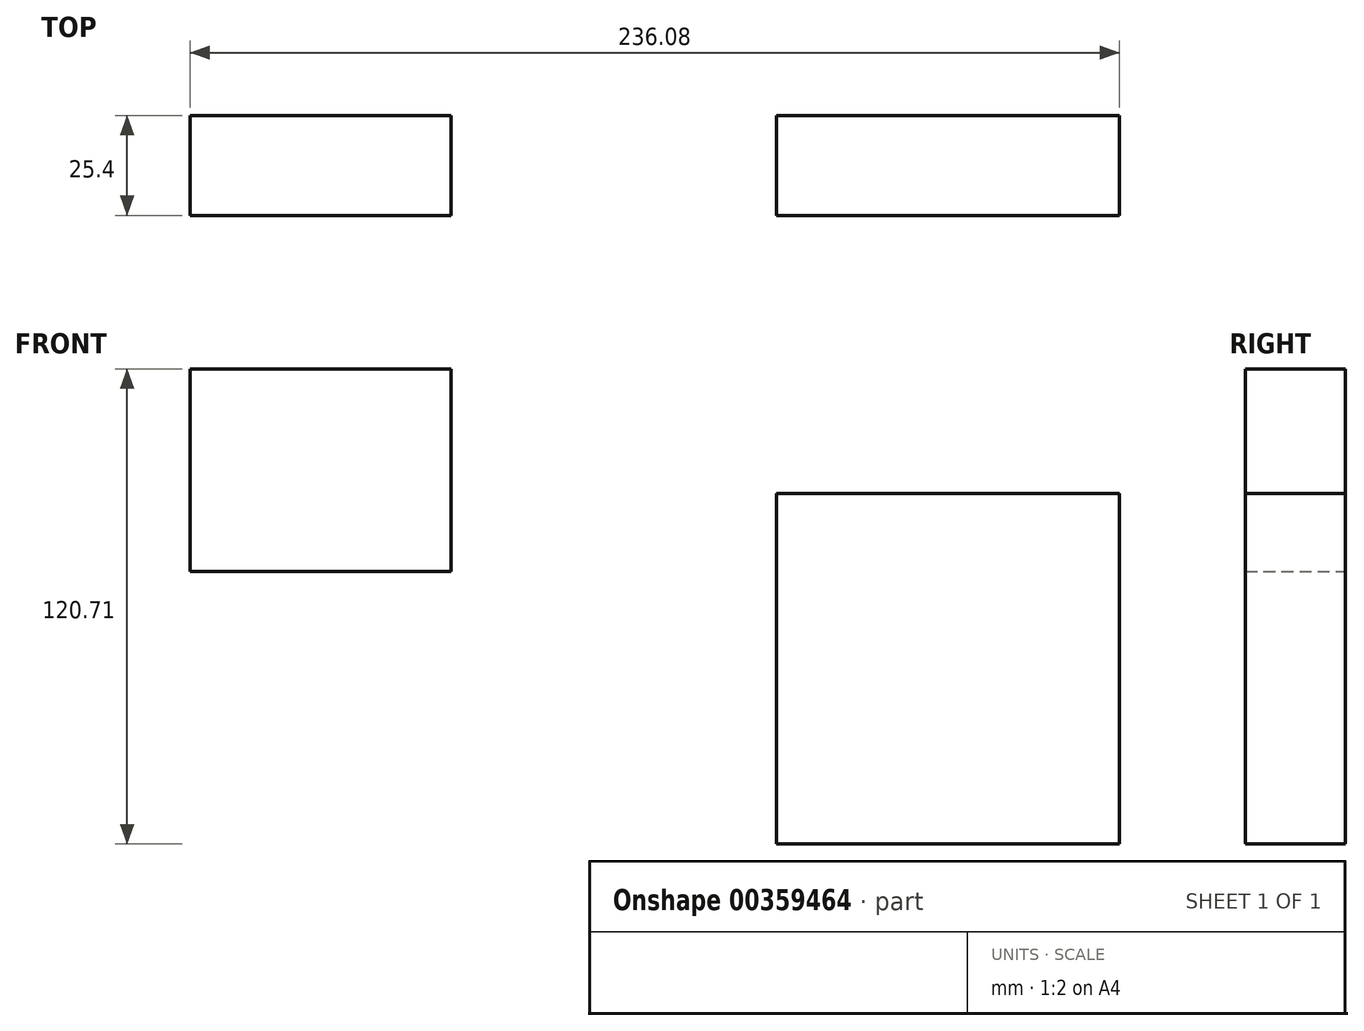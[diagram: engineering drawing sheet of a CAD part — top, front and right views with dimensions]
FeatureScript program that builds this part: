
annotation { "Feature Type Name" : "Feature", "Feature Type Description" : "" }
export const myFeature = defineFeature(function(context is Context, id is Id, definition is map)
    precondition{}
    {
        {
            var Q0;
            Q0=qCreatedBy(makeId("Front.planeOp"),FACE);
            var sketch = newSketch(context, id + "F0", { "sketchPlane" : qUnion([Q0])});
            skLineSegment(sketch, "E0.bottom", {"start": v(-107.24, 69.33) * mm, "end": v(-41, 69.33) * mm});
            skLineSegment(sketch, "E0.top", {"start": v(-107.24, 17.81) * mm, "end": v(-41, 17.81) * mm});
            skLineSegment(sketch, "E0.left", {"start": v(-107.24, 69.33) * mm, "end": v(-107.24, 17.81) * mm});
            skLineSegment(sketch, "E0.right", {"start": v(-41, 69.33) * mm, "end": v(-41, 17.81) * mm});
            skLineSegment(sketch, "E1.bottom", {"start": v(41.73, 37.67) * mm, "end": v(128.84, 37.67) * mm});
            skLineSegment(sketch, "E1.top", {"start": v(41.73, -51.38) * mm, "end": v(128.84, -51.38) * mm});
            skLineSegment(sketch, "E1.left", {"start": v(41.73, 37.67) * mm, "end": v(41.73, -51.38) * mm});
            skLineSegment(sketch, "E1.right", {"start": v(128.84, 37.67) * mm, "end": v(128.84, -51.38) * mm});
            skSolve(sketch);
        }
        {
            var Q0;
            Q0 = qSketchRegion(id + "F0", true);
            extrude(context, id + "F1", {"entities" : qUnion([Q0]), "depth" : 25.4 * mm});
        }
    });
